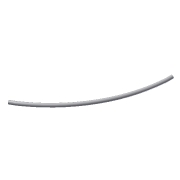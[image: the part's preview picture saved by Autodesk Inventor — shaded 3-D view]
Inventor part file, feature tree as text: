
AUTODESK INVENTOR PART (.ipt)
format: ipt  version: 2016 (Build 200138000, 138)  size: 146,944 bytes
history: native  units: in
note: dims shown in document units (in); Inventor stores cm internally (conversion verified against a paired STEP export)
features: sketch x7, sweep x4, revolve x1
ambient origin geometry x8: Origin, YZ Plane, XZ Plane, XY Plane, X Axis, Y Axis, Z Axis, Center Point
bodies: Solid1 (feature_tree)
feature tree (12):
  revolve  "Revolution1"  [1 undecoded]
  sketch  "Sketch4"  dims[d8=60.0deg d9=0.0638in]
  sweep  "Sweep1"
  sweep  "Sweep2"
  sketch  "Sketch11"  dims[d14=0.0in d15=0.0in d16=0.0in d17=0.0in]
  sweep  "Sweep4"
  sweep  "Sweep5"
  sketch  "Sketch1"  dims[d6=0.8661in d7=33.4252in]
  sketch  "Sketch5"  dims[d10=33.8583in d11=66.8504in]
  sketch  "Sketch6"  dims[d12=0.0257in d13=0.0257in]
  sketch  "Sketch12"  dims[d26=1.5551in]
  sketch  "Sketch13"  dims[d27=0.0in d28=0.0in d30=0.0in d31=0.0in d32=0.6442in d33=1.5551in d34=0.6442in]
note: 1 required parameter value undecoded (feature->parameter linkage not recoverable at this tier; creation-order binding heuristic only, values carry confidence <= 0.55)
